# Revit family: 44380200
name_source: partatom
category: Plumbing Fixtures
revit_build: Autodesk Revit 2018 (Build: 20170223_1515(x64)
units: mm (PartAtom-declared; Revit-internal decimal feet)

## family parameters
Always vertical = Yes
Cut with Voids When Loaded = No
OmniClass Number = 23.45.55.00
OmniClass Title = Sanitary Faucets, Wastes
Part Type = Normal
Room Calculation Point = No
Round Connector Dimension = Use Diameter
Shared = No
Work Plane-Based = No

## types (1)
- 44380200 Overhead shower set
    2D/3D/BIM Files URL = http://static.hansa.com
    3D View = https://static.hansa.com
    Advanced Features = Flexible length / can be shortened
    AssetType = Fixed
    BIMObjectName = 44380200
    Backflow Prevention EN1717 = EB
    BodyMaterial = Brass
    Brand = HANSA
    Catalog Drawing URL = http://static.hansa.com
    Category = Bathroom;Shower
    CloseOffRating = 0
    Color = Chrome
    Connection = Flexible inlet pipes
    Connection Size = G1/2
    Dimension Drawing URL = http://static.hansa.com
    Diverter = Turn operated diverter
    DurationUnit = Year
    EAN Number = 4057304010996
    EN Standard = EN 1112, EN 1113
    ETIM Class Number = EC011383 Shower head
    FDV Document URL = http://www.hansa.com
    FaucetMainMaterial = Brass
    Finish = Polished
    Flow Drawing URL = http://static.hansa.com
    Flow Rate At 300kPa = 250.3 L/s
    FlowCoefficient = 0
    Group = Shower set
    Hand Shower Size = Ø 95 mm
    IfcExportAs = IfcValveType
    IfcExportType = FAUCET
    InletConnectionSize = 15 mm  [stored 0.0492126 ft]
    Installation Type = Wall mounted
    Installation and Maintenance Guide URL = http://static.hansa.com
    Interactive AR View URL = https://static.hansa.com
    Manufacturer = HANSA
    ManufacturerName = HANSA
    ManufacturerURL = http://www.hansa.com
    Market = International;Germany;Austria;Switzerland;Belgium;Netherlands;France;Czech Republic;Slovakia;Hungary;Romania;Italy;Spain;Greece;Portugal;Australia
    Material = Brass
    Max. Hot Water Supply = 70 °C
    Mechanical Parts = Non-return valve(s)
    Mobile Product Information URL = http://mpi.hansa.com
    Model = 44380200 Overhead shower set
    ModelReference = 44380200
    NBSDescription = Shower heads
    NBSReference = 45-35-70/333
    Name = 44380200 Overhead shower set
    Name_en = 44380200 Overhead shower set
    Noise Class = I (ISO 3822)
    NominalDepth = 539 mm
    NominalHeight = 1175 mm
    NominalWidth = 200 mm
    Over Head Shower Size = Ø 200 mm
    Pressure Loss With Flow 02ls = 180000.0 Pa
    Product Code = 44380200
    Product Family = HANSABASICJET
    Product Image URL = http://static.hansa.com
    Product URL = http://static.hansa.com
    Revision = 2
    Sales Package dimensions (LxWxH) = 1154 x 383 x 98
    Shape = Sculptured
    Shower Parts = Hand shower;Shower rail;Overhead shower;Adjustable shower rail bracket;Shower hose (1750 mm);Variable fixing points;Rotatable ball joint connection;Anti limescale technology (easy to clean)
    Shower Spray = Normal;Refreshing;Relaxing
    Shower Spray Number = 3 shower sprays
    Size = 200x540x1175 mm
    Spare-Part Information URL = http://static.hansa.com
    Spout Projection = 407 mm
    Surface treatment = Chrome
    Technical DataSheet URL = http://www.hansa.com
    UNSPSC Class Number = 30181801 Shower head
    URL Declaration of Conformity = http://static.hansa.com
    URL REACH = http://static.hansa.com
    Uniclass2 = Pr_40_30_96_76
    Uniclass2015Description = Shower heads
    Uniclass2015Reference = Pr_40_20_87_76
    Version = 3
    VersionDate = 01/07/2022
    Warranty Information URL = http://warranty.hansa.com
    WarrantyDescription = http://warranty.hansa.com
    WarrantyDurationUnit = Year
    Working Pressure = 100 - 1000 kPa
    WorkingPressure = 100 - 1000 kPa

note: [stored X ft] marks values corroborated as IEEE doubles in the binary element streams (Revit-internal decimal feet)

## geometry (parser evidence)
native form markers: Sweep x6
no freeform markers — native parametric forms only
